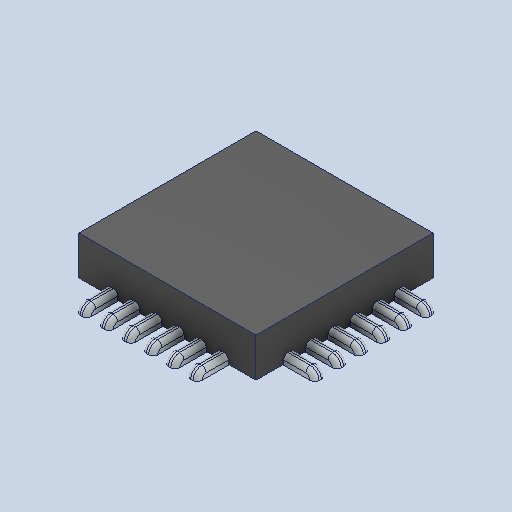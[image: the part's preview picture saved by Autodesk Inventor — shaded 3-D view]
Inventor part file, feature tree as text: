
AUTODESK INVENTOR PART (.ipt)
format: ipt  version: 2024 (Build 280153000, 153)  size: 308,736 bytes
history: native  units: in
note: dims shown in document units (in); Inventor stores cm internally (conversion verified against a paired STEP export)
features: fillet x1
ambient origin geometry x8: Origin, YZ Plane, XZ Plane, XY Plane, X Axis, Y Axis, Z Axis, Center Point
bodies: Solid1 (feature_tree)
feature tree (1):
  fillet  "Fillet3"  [1 undecoded]
note: 1 required parameter value undecoded (feature->parameter linkage not recoverable at this tier; creation-order binding heuristic only, values carry confidence <= 0.55)
